# Revit family: Water_Heaters_HAJDU_HAJDU-SMART_
name_source: partatom
category: Mechanical Equipment
units: mm (PartAtom-declared; Revit-internal decimal feet)

## family parameters
Classification = None
Cut with Voids When Loaded = No
Host = Face
Maintain Annotation Orientation = No
OmniClass Number = 23.31.29.13
OmniClass Title = Hot Water Tank Heaters
Part Type = Normal
Room Calculation Point = No
Round Connector Dimension = Use Diameter
Shared = No

## types (1)
- Nem típus - Terheléstípus katalógus!
    A melegvíz maximális homérséklete = 75 °C
    Csapolási profil = S
    Csatlakozás leírása = Elektromos csatlakozó
    Csatlakozó eltolás = 552 mm  [stored 1.81102 ft]
    Default Elevation = 1219 mm
    Description = Az elektromos, zártrendszerű forróvíztárolók a használati melegvíz igény kielégítésére szolgálnak. A zártrendszerű tárolós vízmelegítők tartálya acéllemezből készül, a korrózió elleni védelmet speciális, titán tartalmú tűzzománc bevonat és aktív magnézium anód biztosítja. Ezek a készülékek több vízvételi hely, illetve zuhanyzós csaptelepek ellátására alkalmasak. A készülékek hőszigetelése freonmentes,  poliuretán szigetelő hab. A fémburkolatú kivitelek nanokerámiás felület előkészítéssel rendelkeznek.

Az új generációs SMART nevű sorozat készülékei Smart Control vezérlésű öntanuló rendszerrel rendelkeznek, melyek segítségével még hatékonyabban és energiatakarékosabban állíthatunk elő használati melegvizet.

Kerámia (szteatitos) fűtőtesttel rendelkezik, aminek nagy előnye a csekély vízkőképződés, a hosszabb éltettartam, és a lényegesen kisebb szervizelési költség.
    Dimenzió "a" = 200 mm  [stored 0.656168 ft]
    Dimenzió "b" = 355 mm
    Dimenzió "c" = 424 mm
    Dimenzió "e" = 236 mm
    Dimenzió "f" = 167 mm  [stored 0.5479 ft]
    Dimenzió "m" = 505 mm  [stored 1.65682 ft]
    Energiahatékonysági osztály = B
    Felfutési ido 15°C-ról 65°C-ra = 0.90 h
    Feszültség = 230 V
    Frekvencia = 50 Hz
    Futobetét típusa = Kerámia
    Futoteljesítmény = 1800 W
    Fázisok száma = 1
    Házház anyaga = Hajdu - Felület - Fehér
    Látszólagos terhelés = 1886 VA
    Magasság = 552 mm  [stored 1.81102 ft]
    Manufacturer = HAJDU
    Model = Modell nincs megadva - Terheléstípus katalógus!
    Névleges urtartalom = 30 l
    Névleges üzemi nyomás = 0.6 MPa
    Product Page URL = https://hajdurt.hu
    Rendeltetés = Zártrendszerű forróvíztároló
    Teljesítménytényezo = 1
    Tömeg = 18.00 kg
    URL = https://hajdurt.hu
    Védettségi fokozat = IPX4
    Vízcsatlakozás = 13 mm
    Z30 = Yes
    Áramfelvétel = 8 A
    Átméro = 410 mm  [stored 1.34514 ft]
    Érintésvédelmi osztály = I.

note: [stored X ft] marks values corroborated as IEEE doubles in the binary element streams (Revit-internal decimal feet)

## geometry (parser evidence)
native form markers: Sweep x7
no freeform markers — native parametric forms only
